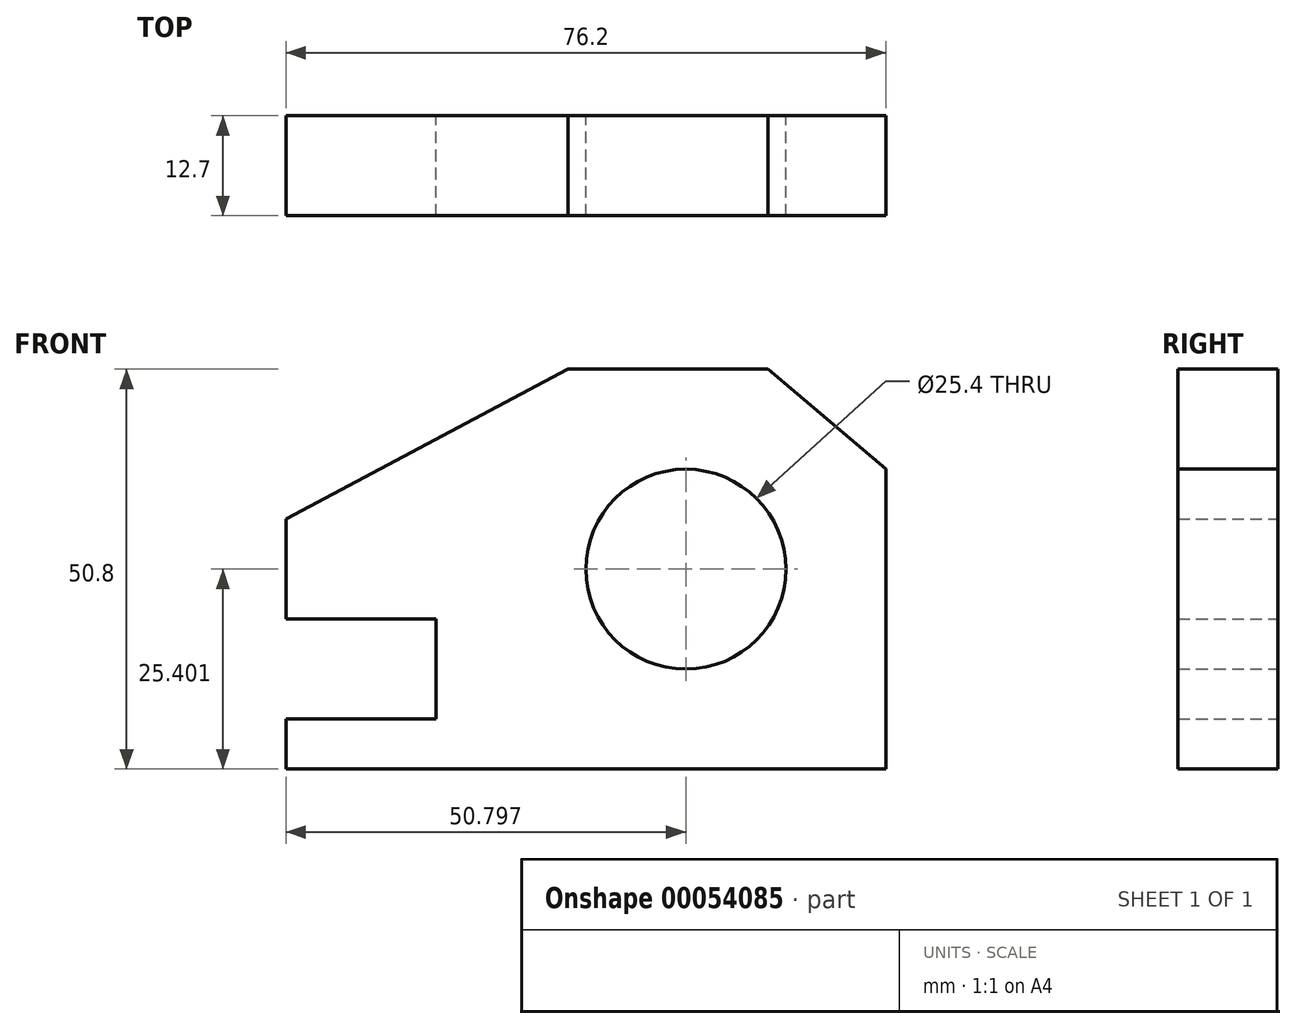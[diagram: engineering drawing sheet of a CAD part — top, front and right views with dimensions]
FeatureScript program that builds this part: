
annotation { "Feature Type Name" : "Feature", "Feature Type Description" : "" }
export const myFeature = defineFeature(function(context is Context, id is Id, definition is map)
    precondition{}
    {
        {
            var Q0;
            Q0=qCreatedBy(makeId("Front.planeOp"),FACE);
            var sketch = newSketch(context, id + "F0", { "sketchPlane" : qUnion([Q0])});
            skLineSegment(sketch, "E0", {"start": v(-13.62, 14.18) * mm, "end": v(11.78, 14.18) * mm});
            skLineSegment(sketch, "E1", {"start": v(11.78, 14.18) * mm, "end": v(26.75, 1.48) * mm});
            skLineSegment(sketch, "E2", {"start": v(26.75, 1.48) * mm, "end": v(26.75, -36.62) * mm});
            skLineSegment(sketch, "E3", {"start": v(26.75, -36.62) * mm, "end": v(-49.45, -36.62) * mm});
            skLineSegment(sketch, "E4", {"start": v(-49.45, -36.62) * mm, "end": v(-49.45, -30.27) * mm});
            skLineSegment(sketch, "E5", {"start": v(-49.45, -30.27) * mm, "end": v(-30.4, -30.27) * mm});
            skLineSegment(sketch, "E6", {"start": v(-30.4, -30.27) * mm, "end": v(-30.4, -17.57) * mm});
            skLineSegment(sketch, "E7", {"start": v(-30.4, -17.57) * mm, "end": v(-49.45, -17.57) * mm});
            skLineSegment(sketch, "E8", {"start": v(-49.45, -17.57) * mm, "end": v(-49.45, -4.87) * mm});
            skLineSegment(sketch, "E9", {"start": v(-49.45, -4.87) * mm, "end": v(-13.62, 14.18) * mm});
            skCircle(sketch, "E10", {"center": v(1.35, -11.22) * mm, "radius": 12.7 * mm});
            skSolve(sketch);
        }
        {
            var Q0;
            Q0 = qSketchRegion(id + "F0", true);
            extrude(context, id + "F1", {"entities" : qUnion([Q0]), "depth" : 12.7 * mm});
        }
    });
